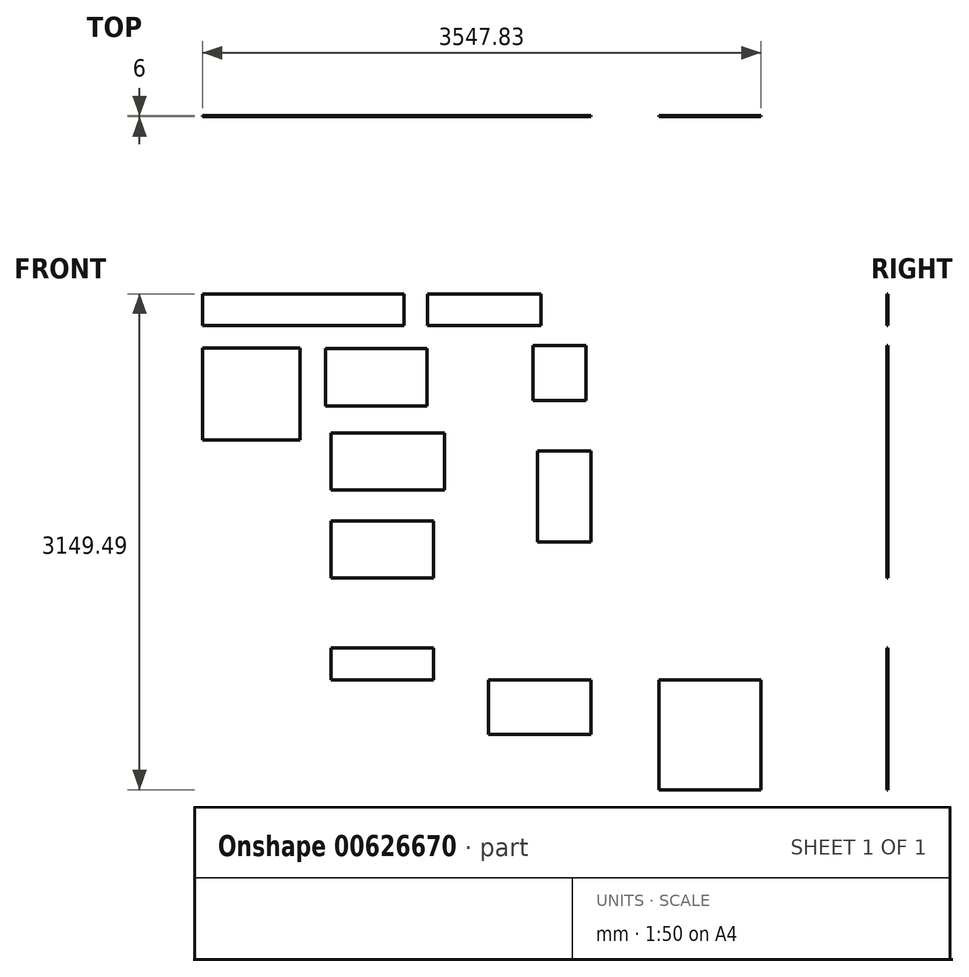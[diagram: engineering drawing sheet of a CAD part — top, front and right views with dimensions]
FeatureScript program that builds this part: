
annotation { "Feature Type Name" : "Feature", "Feature Type Description" : "" }
export const myFeature = defineFeature(function(context is Context, id is Id, definition is map)
    precondition{}
    {
        {
            var Q0;
            Q0=qCreatedBy(makeId("Front.planeOp"),FACE);
            var sketch = newSketch(context, id + "F0", { "sketchPlane" : qUnion([Q0])});
            skLineSegment(sketch, "E0.bottom", {"start": v(-1465.23, 1131.42) * mm, "end": v(-186.23, 1131.42) * mm});
            skLineSegment(sketch, "E0.top", {"start": v(-1465.23, 929.42) * mm, "end": v(-186.23, 929.42) * mm});
            skLineSegment(sketch, "E0.left", {"start": v(-1465.23, 1131.42) * mm, "end": v(-1465.23, 929.42) * mm});
            skLineSegment(sketch, "E0.right", {"start": v(-186.23, 1131.42) * mm, "end": v(-186.23, 929.42) * mm});
            skLineSegment(sketch, "E1.bottom", {"start": v(-35.5, 1131.42) * mm, "end": v(684.5, 1131.42) * mm});
            skLineSegment(sketch, "E1.top", {"start": v(-35.5, 929.42) * mm, "end": v(684.5, 929.42) * mm});
            skLineSegment(sketch, "E1.left", {"start": v(-35.5, 1131.42) * mm, "end": v(-35.5, 929.42) * mm});
            skLineSegment(sketch, "E1.right", {"start": v(684.5, 1131.42) * mm, "end": v(684.5, 929.42) * mm});
            skLineSegment(sketch, "E2.bottom", {"start": v(-1465.23, 786.71) * mm, "end": v(-845.23, 786.71) * mm});
            skLineSegment(sketch, "E2.top", {"start": v(-1465.23, 202.71) * mm, "end": v(-845.23, 202.71) * mm});
            skLineSegment(sketch, "E2.left", {"start": v(-1465.23, 786.71) * mm, "end": v(-1465.23, 202.71) * mm});
            skLineSegment(sketch, "E2.right", {"start": v(-845.23, 786.71) * mm, "end": v(-845.23, 202.71) * mm});
            skLineSegment(sketch, "E3.bottom", {"start": v(-685.74, 782.8) * mm, "end": v(-40.74, 782.8) * mm});
            skLineSegment(sketch, "E3.top", {"start": v(-685.74, 419.8) * mm, "end": v(-40.74, 419.8) * mm});
            skLineSegment(sketch, "E3.left", {"start": v(-685.74, 782.8) * mm, "end": v(-685.74, 419.8) * mm});
            skLineSegment(sketch, "E3.right", {"start": v(-40.74, 782.8) * mm, "end": v(-40.74, 419.8) * mm});
            skLineSegment(sketch, "E4.bottom", {"start": v(-648, 248.4) * mm, "end": v(72, 248.4) * mm});
            skLineSegment(sketch, "E4.top", {"start": v(-648, -114.6) * mm, "end": v(72, -114.6) * mm});
            skLineSegment(sketch, "E4.left", {"start": v(-648, 248.4) * mm, "end": v(-648, -114.6) * mm});
            skLineSegment(sketch, "E4.right", {"start": v(72, 248.4) * mm, "end": v(72, -114.6) * mm});
            skLineSegment(sketch, "E5.bottom", {"start": v(-648, -310.58) * mm, "end": v(0, -310.58) * mm});
            skLineSegment(sketch, "E5.top", {"start": v(-648, -673.58) * mm, "end": v(0, -673.58) * mm});
            skLineSegment(sketch, "E5.left", {"start": v(-648, -310.58) * mm, "end": v(-648, -673.58) * mm});
            skLineSegment(sketch, "E5.right", {"start": v(0, -310.58) * mm, "end": v(0, -673.58) * mm});
            skLineSegment(sketch, "E6.bottom", {"start": v(-648, -1119.07) * mm, "end": v(0, -1119.07) * mm});
            skLineSegment(sketch, "E6.top", {"start": v(-648, -1321.07) * mm, "end": v(0, -1321.07) * mm});
            skLineSegment(sketch, "E6.left", {"start": v(-648, -1119.07) * mm, "end": v(-648, -1321.07) * mm});
            skLineSegment(sketch, "E6.right", {"start": v(0, -1119.07) * mm, "end": v(0, -1321.07) * mm});
            skLineSegment(sketch, "E7.bottom", {"start": v(631.78, 802.7) * mm, "end": v(968.78, 802.7) * mm});
            skLineSegment(sketch, "E7.top", {"start": v(631.78, 453.7) * mm, "end": v(968.78, 453.7) * mm});
            skLineSegment(sketch, "E7.left", {"start": v(631.78, 802.7) * mm, "end": v(631.78, 453.7) * mm});
            skLineSegment(sketch, "E7.right", {"start": v(968.78, 802.7) * mm, "end": v(968.78, 453.7) * mm});
            skLineSegment(sketch, "E8.bottom", {"start": v(661.33, 132.29) * mm, "end": v(1000.33, 132.29) * mm});
            skLineSegment(sketch, "E8.top", {"start": v(661.33, -443.71) * mm, "end": v(1000.33, -443.71) * mm});
            skLineSegment(sketch, "E8.left", {"start": v(661.33, 132.29) * mm, "end": v(661.33, -443.71) * mm});
            skLineSegment(sketch, "E8.right", {"start": v(1000.33, 132.29) * mm, "end": v(1000.33, -443.71) * mm});
            skLineSegment(sketch, "E9.bottom", {"start": v(351.33, -1321.07) * mm, "end": v(1000.33, -1321.07) * mm});
            skLineSegment(sketch, "E9.top", {"start": v(351.33, -1668.07) * mm, "end": v(1000.33, -1668.07) * mm});
            skLineSegment(sketch, "E9.left", {"start": v(351.33, -1321.07) * mm, "end": v(351.33, -1668.07) * mm});
            skLineSegment(sketch, "E9.right", {"start": v(1000.33, -1321.07) * mm, "end": v(1000.33, -1668.07) * mm});
            skLineSegment(sketch, "E10.bottom", {"start": v(1434.6, -1321.07) * mm, "end": v(2082.6, -1321.07) * mm});
            skLineSegment(sketch, "E10.top", {"start": v(1434.6, -2018.07) * mm, "end": v(2082.6, -2018.07) * mm});
            skLineSegment(sketch, "E10.left", {"start": v(1434.6, -1321.07) * mm, "end": v(1434.6, -2018.07) * mm});
            skLineSegment(sketch, "E10.right", {"start": v(2082.6, -1321.07) * mm, "end": v(2082.6, -2018.07) * mm});
            skSolve(sketch);
        }
        {
            var Q0;
            Q0 = qSketchRegion(id + "F0", true);
            extrude(context, id + "F1", {"entities" : qUnion([Q0]), "depth" : 6 * mm, "offsetDistance" : 25 * mm});
        }
    });
